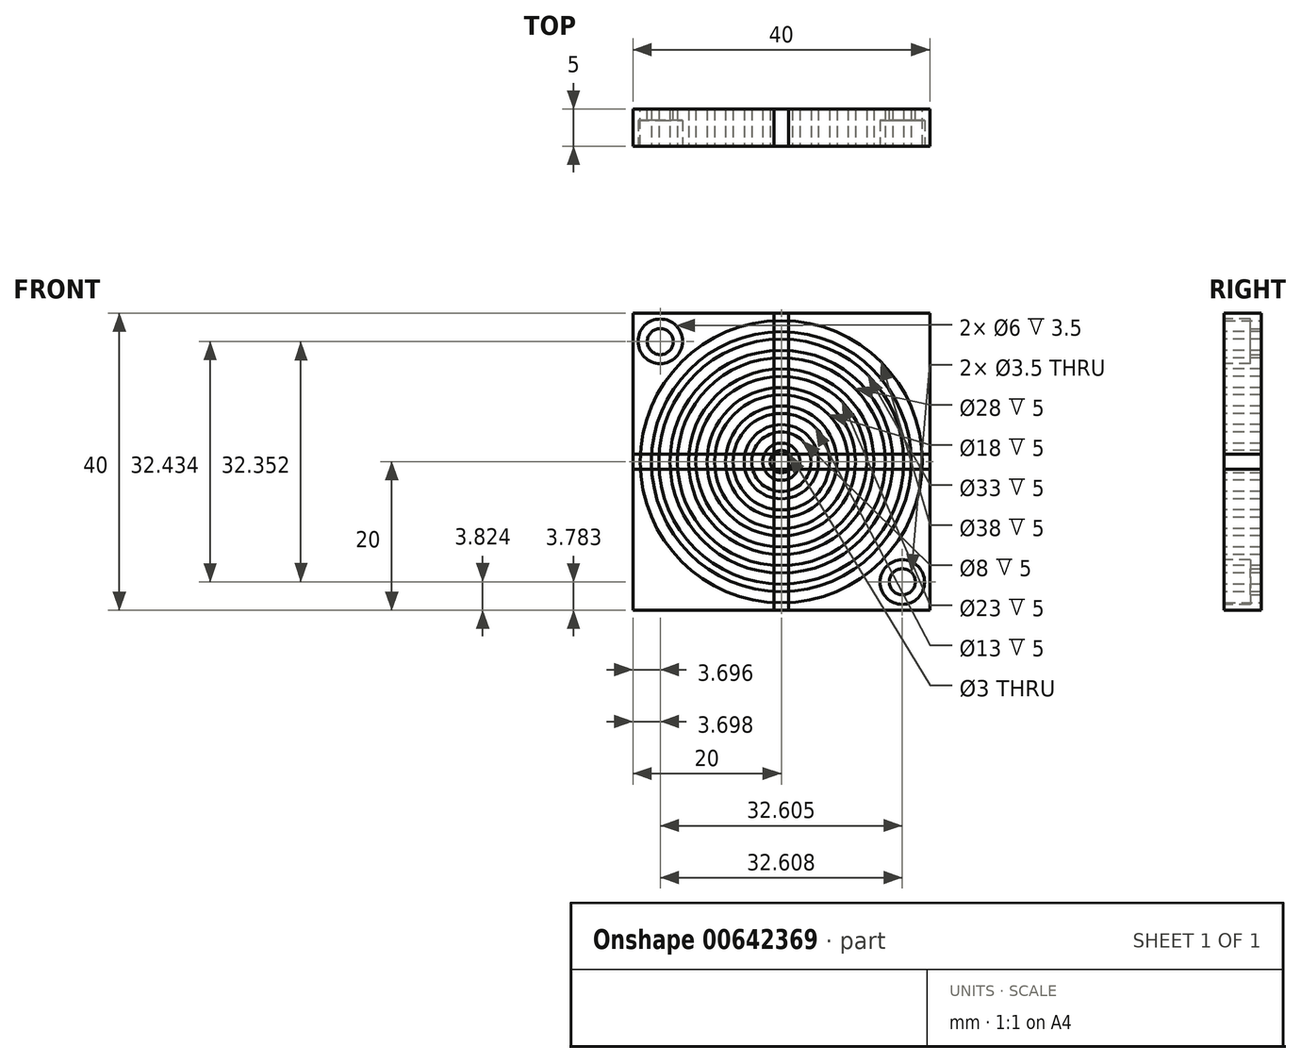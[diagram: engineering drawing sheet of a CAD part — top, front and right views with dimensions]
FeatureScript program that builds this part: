
annotation { "Feature Type Name" : "Feature", "Feature Type Description" : "" }
export const myFeature = defineFeature(function(context is Context, id is Id, definition is map)
    precondition{}
    {
        {
            var Q0;
            Q0=qCreatedBy(makeId("Front.planeOp"),FACE);
            var sketch = newSketch(context, id + "F0", { "sketchPlane" : qUnion([Q0])});
            skLineSegment(sketch, "E0.bottom", {"start": v(-20, 20) * mm, "end": v(20, 20) * mm});
            skLineSegment(sketch, "E0.top", {"start": v(-20, -20) * mm, "end": v(20, -20) * mm});
            skLineSegment(sketch, "E0.left", {"start": v(-20, 20) * mm, "end": v(-20, -20) * mm});
            skLineSegment(sketch, "E0.right", {"start": v(20, 20) * mm, "end": v(20, -20) * mm});
            skPoint(sketch, "E0.middle", {"position": v(0, 0) * mm});
            skCircle(sketch, "E1", {"center": v(0, 0) * mm, "radius": 19 * mm});
            skSolve(sketch);
        }
        {
            var Q0;
            Q0 = qSketchRegion(id + "F0", true);
            extrude(context, id + "F1", {"entities" : qUnion([Q0]), "depth" : 5 * mm, "offsetDistance" : 25 * mm});
        }
        {
            var Q0;
            Q0=makeQuery(id+"F1.opExtrude","CAP_FACE",FACE,{"disambiguationData":[OSD([sQuery(id+"F0.wireOp",EDGE,"E0.bottom"),sQuery(id+"F0.wireOp",EDGE,"E0.top"),sQuery(id+"F0.wireOp",EDGE,"E0.left"),sQuery(id+"F0.wireOp",EDGE,"E0.right"),sQuery(id+"F0.wireOp",EDGE,"E1")])],"isStart":false});
            var sketch = newSketch(context, id + "F2", { "sketchPlane" : qUnion([Q0])});
            skCircle(sketch, "E2", {"center": v(-16.3, 16.22) * mm, "radius": 3 * mm});
            skSolve(sketch);
        }
        {
            var Q0;
            Q0=makeQuery(id+"F1.opExtrude","CAP_FACE",FACE,{"disambiguationData":[OSD([sQuery(id+"F0.wireOp",EDGE,"E0.bottom"),sQuery(id+"F0.wireOp",EDGE,"E0.top"),sQuery(id+"F0.wireOp",EDGE,"E0.left"),sQuery(id+"F0.wireOp",EDGE,"E0.right"),sQuery(id+"F0.wireOp",EDGE,"E1")])],"isStart":true});
            var sketch = newSketch(context, id + "F3", { "sketchPlane" : qUnion([Q0])});
            skCircle(sketch, "E3", {"center": v(16.3, 16.18) * mm, "radius": 1.75 * mm});
            skSolve(sketch);
        }
        {
            var Q0;
            Q0 = qSketchRegion(id + "F3", true);
            extrude(context, id + "F4", {"entities" : qUnion([Q0]), "oppositeDirection" : true, "depth" : 5 * mm, "offsetDistance" : 25 * mm});
        }
        {
            var Q0;
            Q0 = qSketchRegion(id + "F2", true);
            extrude(context, id + "F5", {"entities" : qUnion([Q0]), "oppositeDirection" : true, "depth" : 3.5 * mm, "offsetDistance" : 25 * mm});
        }
        {
            var Q0;
            Q0=qCreatedBy(makeId("Top.planeOp"),FACE);
            var sketch = newSketch(context, id + "F6", { "sketchPlane" : qUnion([Q0])});
            skLineSegment(sketch, "E4", {"start": v(0, 9.6) * mm, "end": v(0, -20.04) * mm});
            skSolve(sketch);
        }
        {
            var Q0;
            Q0=makeQuery(id+"F4.opExtrude","SWEPT_BODY",BODY,{"disambiguationData":[OSD([sQuery(id+"F3.wireOp",EDGE,"E3")])]});
            var Q1;
            Q1=makeQuery(id+"F5.opExtrude","SWEPT_BODY",BODY,{"disambiguationData":[OSD([sQuery(id+"F2.wireOp",EDGE,"E2")])]});
            var Q2;
            Q2=sQuery(id+"F6.wireOp",EDGE,"E4");
            circularPattern(context, id + "F7", {"entities" : qUnion([Q0, Q1]), "axis" : qUnion([Q2]), "angle" : 360 * degree, "instanceCount" : 2, "equalSpace" : true});
        }
        {
            var Q0;
            Q0=makeQuery(id+"F7.opPattern","COPY",BODY,{"derivedFrom":makeQuery(id+"F5.opExtrude","SWEPT_BODY",BODY,{"disambiguationData":[OSD([sQuery(id+"F2.wireOp",EDGE,"E2")])]}),"instanceName":"1"});
            var Q1;
            Q1=makeQuery(id+"F7.opPattern","COPY",BODY,{"derivedFrom":makeQuery(id+"F4.opExtrude","SWEPT_BODY",BODY,{"disambiguationData":[OSD([sQuery(id+"F3.wireOp",EDGE,"E3")])]}),"instanceName":"1"});
            var Q2;
            Q2=makeQuery(id+"F5.opExtrude","SWEPT_BODY",BODY,{"disambiguationData":[OSD([sQuery(id+"F2.wireOp",EDGE,"E2")])]});
            var Q3;
            Q3=makeQuery(id+"F4.opExtrude","SWEPT_BODY",BODY,{"disambiguationData":[OSD([sQuery(id+"F3.wireOp",EDGE,"E3")])]});
            var Q4;
            Q4=makeQuery(id+"F1.opExtrude","SWEPT_BODY",BODY,{"disambiguationData":[OSD([sQuery(id+"F0.wireOp",EDGE,"E0.bottom"),sQuery(id+"F0.wireOp",EDGE,"E0.top"),sQuery(id+"F0.wireOp",EDGE,"E0.left"),sQuery(id+"F0.wireOp",EDGE,"E0.right"),sQuery(id+"F0.wireOp",EDGE,"E1")])]});
            booleanBodies(context, id + "F8", {"operationType" : BooleanOperationType.SUBTRACTION, "tools" : qUnion([Q0, Q1, Q2, Q3]), "targets" : qUnion([Q4])});
        }
        {
            var Q0;
            Q0=makeQuery(id+"F1.opExtrude","CAP_FACE",FACE,{"disambiguationData":[OSD([sQuery(id+"F0.wireOp",EDGE,"E0.bottom"),sQuery(id+"F0.wireOp",EDGE,"E0.top"),sQuery(id+"F0.wireOp",EDGE,"E0.left"),sQuery(id+"F0.wireOp",EDGE,"E0.right"),sQuery(id+"F0.wireOp",EDGE,"E1")])],"isStart":false});
            var sketch = newSketch(context, id + "F9", { "sketchPlane" : qUnion([Q0])});
            skCircle(sketch, "E5", {"center": v(0, 0) * mm, "radius": 9 * mm});
            skCircle(sketch, "E6", {"center": v(0, 0) * mm, "radius": 10 * mm});
            skSolve(sketch);
        }
        {
            var Q0;
            Q0=makeQuery(id+"F9.imprint","IMPRINT",FACE,{"disambiguationData":[TD([[makeQuery(id+"F9.imprint","IMPRINT",EDGE,{"derivedFrom":makeQuery(id+"F1.opExtrude","CAP_EDGE",EDGE,{"disambiguationData":[OSD([sQuery(id+"F0.wireOp",EDGE,"E0.bottom")])],"isStart":false})}),-1.0]])]});
            var sketch = newSketch(context, id + "F10", { "sketchPlane" : qUnion([Q0])});
            skCircle(sketch, "E7", {"center": v(0, 0) * mm, "radius": 4 * mm});
            skCircle(sketch, "E8", {"center": v(0, 0) * mm, "radius": 5 * mm});
            skSolve(sketch);
        }
        {
            var Q0;
            Q0=makeQuery(id+"F9.imprint","IMPRINT",FACE,{"disambiguationData":[TD([[makeQuery(id+"F9.imprint","IMPRINT",EDGE,{"derivedFrom":makeQuery(id+"F1.opExtrude","CAP_EDGE",EDGE,{"disambiguationData":[OSD([sQuery(id+"F0.wireOp",EDGE,"E0.bottom")])],"isStart":false})}),-1.0]])]});
            var sketch = newSketch(context, id + "F11", { "sketchPlane" : qUnion([Q0])});
            skCircle(sketch, "E9", {"center": v(0, 0) * mm, "radius": 6.5 * mm});
            skCircle(sketch, "E10", {"center": v(0, 0) * mm, "radius": 7.5 * mm});
            skSolve(sketch);
        }
        {
            var Q0;
            Q0=makeQuery(id+"F9.imprint","IMPRINT",FACE,{"disambiguationData":[TD([[makeQuery(id+"F9.imprint","IMPRINT",EDGE,{"derivedFrom":makeQuery(id+"F1.opExtrude","CAP_EDGE",EDGE,{"disambiguationData":[OSD([sQuery(id+"F0.wireOp",EDGE,"E0.bottom")])],"isStart":false})}),-1.0]])]});
            var sketch = newSketch(context, id + "F12", { "sketchPlane" : qUnion([Q0])});
            skCircle(sketch, "E11", {"center": v(0, 0) * mm, "radius": 1.5 * mm});
            skCircle(sketch, "E12", {"center": v(0, 0) * mm, "radius": 2.5 * mm});
            skSolve(sketch);
        }
        {
            var Q0;
            Q0=makeQuery(id+"F10.imprint","IMPRINT",FACE,{"disambiguationData":[TD([[makeQuery(id+"F10.imprint","IMPRINT",EDGE,{"derivedFrom":makeQuery(id+"F9.imprint","IMPRINT",EDGE,{"derivedFrom":makeQuery(id+"F1.opExtrude","CAP_EDGE",EDGE,{"disambiguationData":[OSD([sQuery(id+"F0.wireOp",EDGE,"E0.bottom")])],"isStart":false})})}),-1.0]])]});
            var sketch = newSketch(context, id + "F13", { "sketchPlane" : qUnion([Q0])});
            skCircle(sketch, "E13", {"center": v(0, 0) * mm, "radius": 2.5 * mm});
            skSolve(sketch);
        }
        {
            var Q0;
            Q0=makeQuery(id+"F9.imprint","IMPRINT",FACE,{"disambiguationData":[TD([[makeQuery(id+"F9.imprint","IMPRINT",EDGE,{"derivedFrom":makeQuery(id+"F1.opExtrude","CAP_EDGE",EDGE,{"disambiguationData":[OSD([sQuery(id+"F0.wireOp",EDGE,"E0.bottom")])],"isStart":false})}),-1.0]])]});
            var sketch = newSketch(context, id + "F14", { "sketchPlane" : qUnion([Q0])});
            skCircle(sketch, "E14", {"center": v(0, 0) * mm, "radius": 11.5 * mm});
            skCircle(sketch, "E15", {"center": v(0, 0) * mm, "radius": 12.5 * mm});
            skSolve(sketch);
        }
        {
            var Q0;
            Q0=makeQuery(id+"F9.imprint","IMPRINT",FACE,{"disambiguationData":[TD([[makeQuery(id+"F9.imprint","IMPRINT",EDGE,{"derivedFrom":makeQuery(id+"F1.opExtrude","CAP_EDGE",EDGE,{"disambiguationData":[OSD([sQuery(id+"F0.wireOp",EDGE,"E0.bottom")])],"isStart":false})}),-1.0]])]});
            var sketch = newSketch(context, id + "F15", { "sketchPlane" : qUnion([Q0])});
            skCircle(sketch, "E16", {"center": v(0, 0) * mm, "radius": 14 * mm});
            skCircle(sketch, "E17", {"center": v(0, 0) * mm, "radius": 15 * mm});
            skSolve(sketch);
        }
        {
            var Q0;
            Q0=makeQuery(id+"F9.imprint","IMPRINT",FACE,{"disambiguationData":[TD([[makeQuery(id+"F9.imprint","IMPRINT",EDGE,{"derivedFrom":makeQuery(id+"F1.opExtrude","CAP_EDGE",EDGE,{"disambiguationData":[OSD([sQuery(id+"F0.wireOp",EDGE,"E0.bottom")])],"isStart":false})}),-1.0]])]});
            var sketch = newSketch(context, id + "F16", { "sketchPlane" : qUnion([Q0])});
            skCircle(sketch, "E18", {"center": v(0, 0) * mm, "radius": 16.5 * mm});
            skCircle(sketch, "E19", {"center": v(0, 0) * mm, "radius": 17.5 * mm});
            skSolve(sketch);
        }
        {
            var Q0;
            Q0=makeQuery(id+"F1.opExtrude","CAP_FACE",FACE,{"disambiguationData":[OSD([sQuery(id+"F0.wireOp",EDGE,"E0.bottom"),sQuery(id+"F0.wireOp",EDGE,"E0.top"),sQuery(id+"F0.wireOp",EDGE,"E0.left"),sQuery(id+"F0.wireOp",EDGE,"E0.right"),sQuery(id+"F0.wireOp",EDGE,"E1")])],"isStart":false});
            var sketch = newSketch(context, id + "F17", { "sketchPlane" : qUnion([Q0])});
            skLineSegment(sketch, "E20.bottom", {"start": v(-1, 20) * mm, "end": v(1, 20) * mm});
            skLineSegment(sketch, "E20.top", {"start": v(-1, -20) * mm, "end": v(1, -20) * mm});
            skLineSegment(sketch, "E20.left", {"start": v(-1, 20) * mm, "end": v(-1, -20) * mm});
            skLineSegment(sketch, "E20.right", {"start": v(1, 20) * mm, "end": v(1, -20) * mm});
            skPoint(sketch, "E20.middle", {"position": v(0, 0) * mm});
            skSolve(sketch);
        }
        {
            var Q0;
            {var subQ0=makeQuery(id+"F1.opExtrude","CAP_EDGE",EDGE,{"disambiguationData":[OSD([sQuery(id+"F0.wireOp",EDGE,"E0.right")])],"isStart":false});Q0=makeQuery(id+"F17.imprint","IMPRINT",FACE,{"disambiguationData":[TD([[makeQuery(id+"F17.imprint","IMPRINT",EDGE,{"derivedFrom":subQ0}),-1.0]])]});}
            var sketch = newSketch(context, id + "F18", { "sketchPlane" : qUnion([Q0])});
            skLineSegment(sketch, "E21.bottom", {"start": v(-20, 1) * mm, "end": v(20, 1) * mm});
            skLineSegment(sketch, "E21.top", {"start": v(-20, -1) * mm, "end": v(20, -1) * mm});
            skLineSegment(sketch, "E21.left", {"start": v(-20, 1) * mm, "end": v(-20, -1) * mm});
            skLineSegment(sketch, "E21.right", {"start": v(20, 1) * mm, "end": v(20, -1) * mm});
            skPoint(sketch, "E21.middle", {"position": v(0, 0) * mm});
            skSolve(sketch);
        }
        {
            var Q0;
            Q0 = qSketchRegion(id + "F9", true);
            var Q1;
            Q1 = qSketchRegion(id + "F10", true);
            var Q2;
            Q2 = qSketchRegion(id + "F11", true);
            var Q3;
            Q3 = qSketchRegion(id + "F12", true);
            var Q4;
            Q4 = qSketchRegion(id + "F13", true);
            var Q5;
            Q5 = qSketchRegion(id + "F14", true);
            var Q6;
            Q6 = qSketchRegion(id + "F15", true);
            var Q7;
            Q7 = qSketchRegion(id + "F16", true);
            var Q8;
            Q8 = qSketchRegion(id + "F17", true);
            var Q9;
            Q9 = qSketchRegion(id + "F18", true);
            extrude(context, id + "F19", {"entities" : qUnion([Q0, Q1, Q2, Q3, Q4, Q5, Q6, Q7, Q8, Q9]), "oppositeDirection" : true, "depth" : 5 * mm, "offsetDistance" : 25 * mm});
        }
    });
